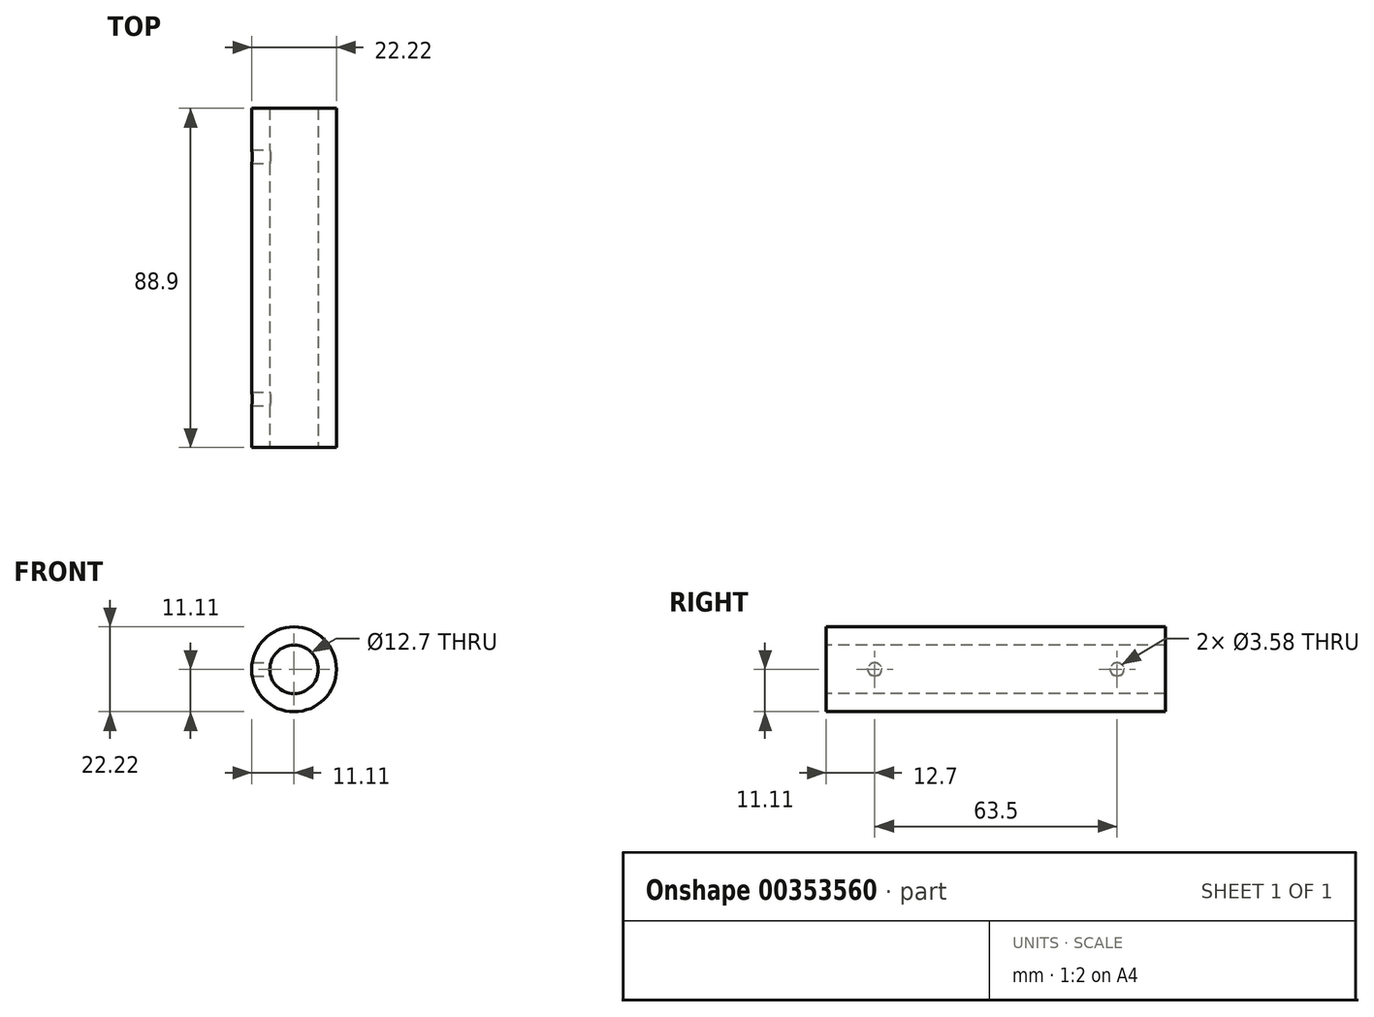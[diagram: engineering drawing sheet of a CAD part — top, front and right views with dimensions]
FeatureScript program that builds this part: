
annotation { "Feature Type Name" : "Feature", "Feature Type Description" : "" }
export const myFeature = defineFeature(function(context is Context, id is Id, definition is map)
    precondition{}
    {
        {
            var Q0;
            Q0=qCreatedBy(makeId("Front.planeOp"),FACE);
            var sketch = newSketch(context, id + "F0", { "sketchPlane" : qUnion([Q0])});
            skCircle(sketch, "E0", {"center": v(0, 0) * mm, "radius": 11.11 * mm});
            skSolve(sketch);
        }
        {
            var Q0;
            Q0 = qSketchRegion(id + "F0", true);
            extrude(context, id + "F1", {"entities" : qUnion([Q0]), "depth" : 88.9 * mm, "symmetric" : true});
        }
        {
            var Q0;
            Q0=makeQuery(id+"F1.opExtrude","CAP_FACE",FACE,{"disambiguationData":[OSD([sQuery(id+"F0.wireOp",EDGE,"E0")])],"isStart":false});
            var sketch = newSketch(context, id + "F2", { "sketchPlane" : qUnion([Q0])});
            skCircle(sketch, "E1", {"center": v(0, 0) * mm, "radius": 6.35 * mm});
            skSolve(sketch);
        }
        {
            var Q0;
            Q0 = qSketchRegion(id + "F2", true);
            extrude(context, id + "F3", {"entities" : qUnion([Q0]), "operationType" : NewBodyOperationType.REMOVE, "oppositeDirection" : true, "depth" : 88.9 * mm});
        }
        {
            var Q0;
            Q0=qCreatedBy(makeId("Right.planeOp"),FACE);
            var sketch = newSketch(context, id + "F4", { "sketchPlane" : qUnion([Q0])});
            skCircle(sketch, "E2", {"center": v(-31.75, 0) * mm, "radius": 1.8 * mm});
            skSolve(sketch);
        }
        {
            var Q0;
            Q0 = qSketchRegion(id + "F4", true);
            extrude(context, id + "F5", {"entities" : qUnion([Q0]), "operationType" : NewBodyOperationType.REMOVE, "endBound" : BoundingType.THROUGH_ALL, "oppositeDirection" : true, "depth" : 12.7 * mm});
        }
        {
            var Q0;
            Q0=qCreatedBy(makeId("Right.planeOp"),FACE);
            var sketch = newSketch(context, id + "F6", { "sketchPlane" : qUnion([Q0])});
            skCircle(sketch, "E3", {"center": v(31.75, 0) * mm, "radius": 1.8 * mm});
            skSolve(sketch);
        }
        {
            var Q0;
            Q0 = qSketchRegion(id + "F6", true);
            extrude(context, id + "F7", {"entities" : qUnion([Q0]), "operationType" : NewBodyOperationType.REMOVE, "endBound" : BoundingType.THROUGH_ALL, "oppositeDirection" : true, "depth" : 22.22 * mm});
        }
    });
